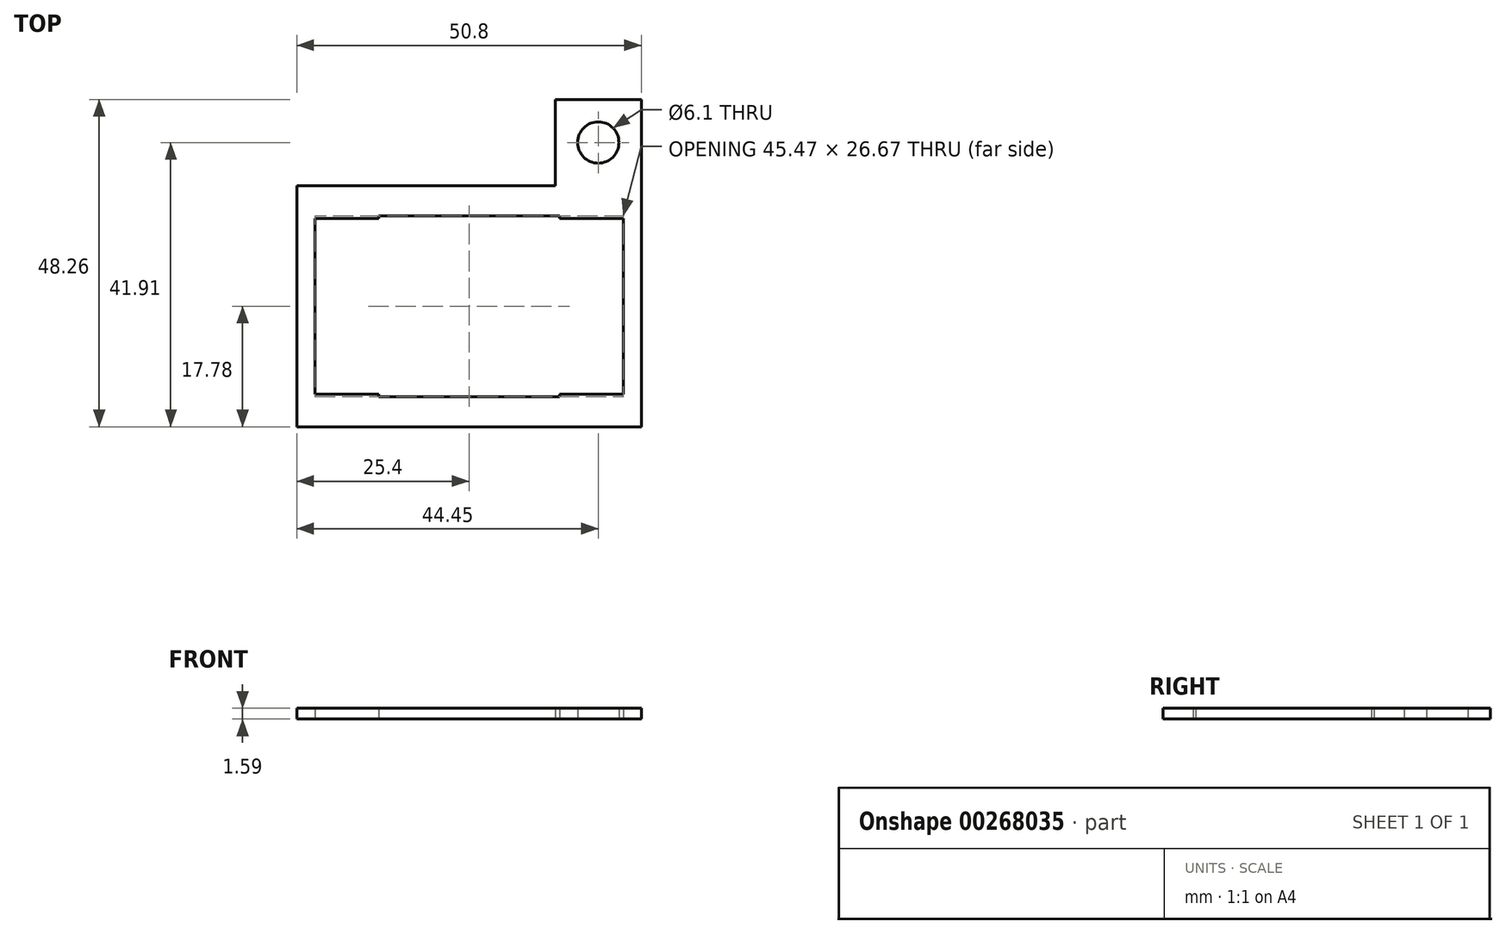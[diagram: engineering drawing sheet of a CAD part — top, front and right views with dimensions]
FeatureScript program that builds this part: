
annotation { "Feature Type Name" : "Feature", "Feature Type Description" : "" }
export const myFeature = defineFeature(function(context is Context, id is Id, definition is map)
    precondition{}
    {
        {
            var Q0;
            Q0=qCreatedBy(makeId("Top.planeOp"),FACE);
            var sketch = newSketch(context, id + "F0", { "sketchPlane" : qUnion([Q0])});
            skLineSegment(sketch, "E0.bottom", {"start": v(25.4, -17.78) * mm, "end": v(-25.4, -17.78) * mm});
            skLineSegment(sketch, "E0.top", {"start": v(25.4, 17.78) * mm, "end": v(-25.4, 17.78) * mm});
            skLineSegment(sketch, "E0.left", {"start": v(25.4, -17.78) * mm, "end": v(25.4, 17.78) * mm});
            skLineSegment(sketch, "E0.right", {"start": v(-25.4, -17.78) * mm, "end": v(-25.4, 17.78) * mm});
            skPoint(sketch, "E0.middle", {"position": v(0, 0) * mm});
            skLineSegment(sketch, "E1.bottom", {"start": v(22.73, -12.95) * mm, "end": v(-22.73, -12.95) * mm});
            skLineSegment(sketch, "E1.top", {"start": v(22.73, 12.95) * mm, "end": v(-22.73, 12.95) * mm});
            skLineSegment(sketch, "E1.left", {"start": v(22.73, -12.95) * mm, "end": v(22.73, 12.95) * mm});
            skLineSegment(sketch, "E1.right", {"start": v(-22.73, -12.95) * mm, "end": v(-22.73, 12.95) * mm});
            skLineSegment(sketch, "E2.bottom", {"start": v(13.33, -13.33) * mm, "end": v(-13.34, -13.34) * mm});
            skLineSegment(sketch, "E2.top", {"start": v(13.34, 13.34) * mm, "end": v(-13.33, 13.33) * mm});
            skLineSegment(sketch, "E2.left", {"start": v(13.33, -13.33) * mm, "end": v(13.34, 13.34) * mm});
            skLineSegment(sketch, "E2.right", {"start": v(-13.34, -13.34) * mm, "end": v(-13.33, 13.33) * mm});
            skLineSegment(sketch, "E3.bottom", {"start": v(25.4, 17.78) * mm, "end": v(12.7, 17.78) * mm});
            skLineSegment(sketch, "E3.top", {"start": v(25.4, 30.48) * mm, "end": v(12.7, 30.48) * mm});
            skLineSegment(sketch, "E3.left", {"start": v(25.4, 17.78) * mm, "end": v(25.4, 30.48) * mm});
            skLineSegment(sketch, "E3.right", {"start": v(12.7, 17.78) * mm, "end": v(12.7, 30.48) * mm});
            skLineSegment(sketch, "E4", {"start": v(25.4, 30.48) * mm, "end": v(12.7, 17.78) * mm, "construction": true});
            skCircle(sketch, "E5", {"center": v(19.05, 24.13) * mm, "radius": 3.05 * mm});
            skSolve(sketch);
        }
        {
            var Q0;
            Q0 = qSketchRegion(id + "F0", true);
            extrude(context, id + "F1", {"entities" : qUnion([Q0]), "depth" : 1.59 * mm, "offsetDistance" : 25.4 * mm});
        }
    });
